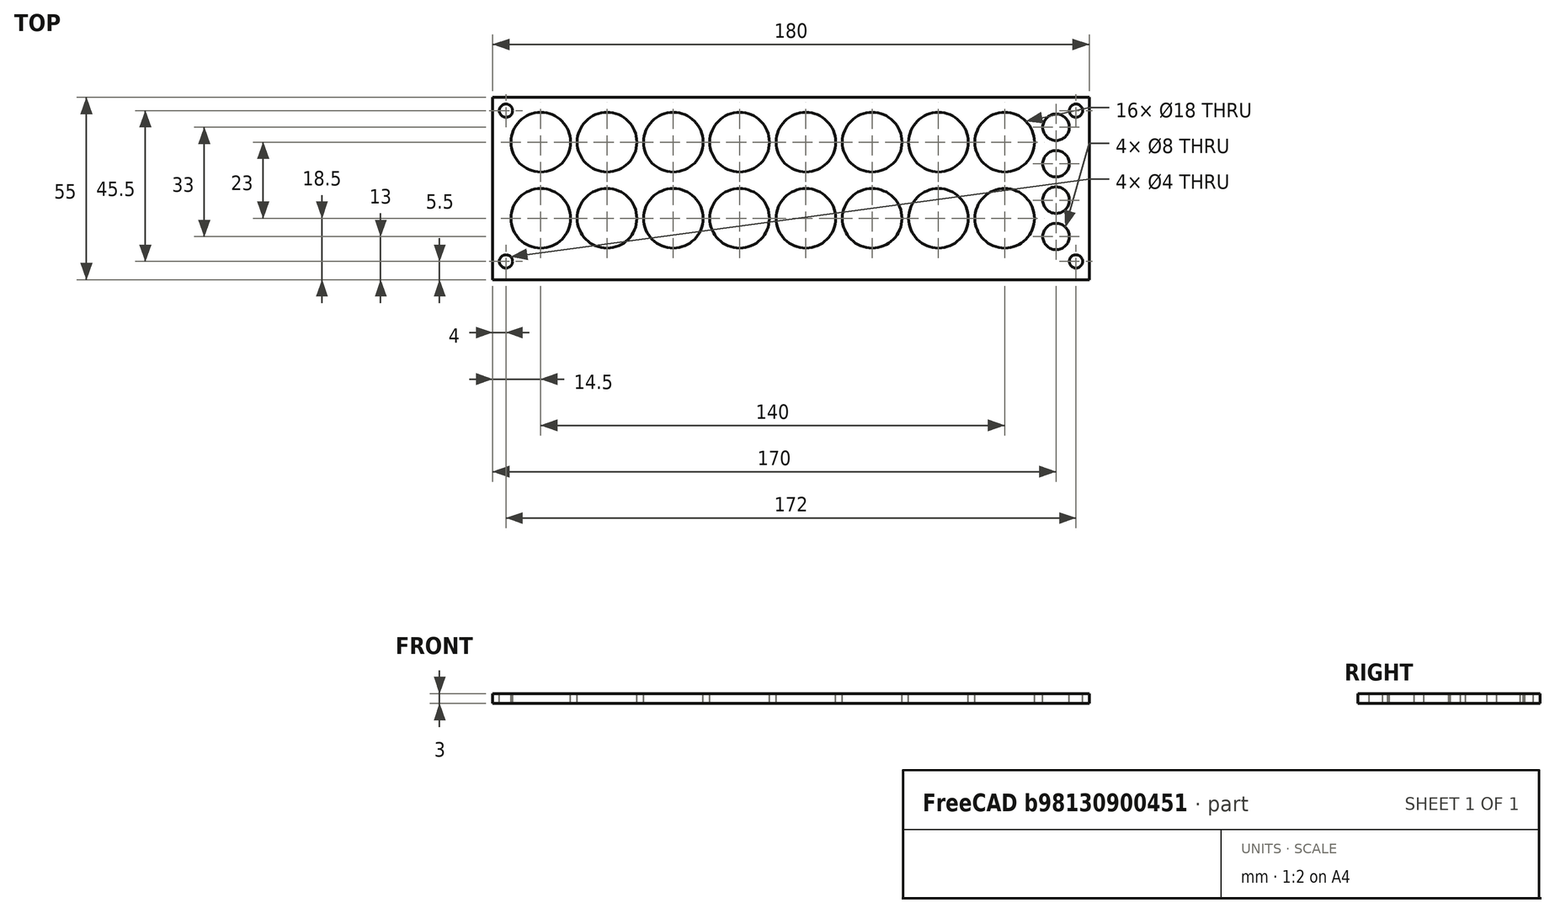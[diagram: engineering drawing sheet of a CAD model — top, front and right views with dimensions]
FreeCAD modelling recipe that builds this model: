
FCSTD DOCUMENT  (FreeCAD 0.17R13509 (Git))
Label: 工具台-2
License: All rights reserved
LicenseURL: http://en.wikipedia.org/wiki/All_rights_reserved
objects: Part::Cylinder×24, Part::Cut×24, Part::Box×1
note: 49 computed .brp shape members not serialized (recipe doc carries the construction recipe); baked Part::Feature solids carry a one-line shape summary decoded from their .brp

FEATURE [Part::Box] Box  label="外壳"
  AttacherType = Attacher::AttachEngine3D
  Height = 3
  Length = 180
  Width = 55
FEATURE [Part::Cylinder] Cylinder  label="圆柱体1.1"
  Angle = 360
  AttacherType = Attacher::AttachEngine3D
  Height = 3
  Placement = pos=(14.5,41.5,0) rot=(0,0,1;0rad)
  Radius = 9
FEATURE [Part::Cylinder] Cylinder001  label="圆柱体1.2"
  Angle = 360
  AttacherType = Attacher::AttachEngine3D
  Height = 3
  Placement = pos=(34.5,41.5,0) rot=(0,0,1;0rad)
  Radius = 9
FEATURE [Part::Cylinder] Cylinder002  label="圆柱体1.3"
  Angle = 360
  AttacherType = Attacher::AttachEngine3D
  Height = 3
  Placement = pos=(54.5,41.5,0) rot=(0,0,1;0rad)
  Radius = 9
FEATURE [Part::Cylinder] Cylinder003  label="圆柱体1.4"
  Angle = 360
  AttacherType = Attacher::AttachEngine3D
  Height = 3
  Placement = pos=(74.5,41.5,0) rot=(0,0,1;0rad)
  Radius = 9
FEATURE [Part::Cylinder] Cylinder004  label="圆柱体2.1"
  Angle = 360
  AttacherType = Attacher::AttachEngine3D
  Height = 3
  Placement = pos=(14.5,18.5,0) rot=(0,0,1;0rad)
  Radius = 9
FEATURE [Part::Cylinder] Cylinder005  label="圆柱体2.2"
  Angle = 360
  AttacherType = Attacher::AttachEngine3D
  Height = 3
  Placement = pos=(34.5,18.5,0) rot=(0,0,1;0rad)
  Radius = 9
FEATURE [Part::Cylinder] Cylinder006  label="圆柱体2.3"
  Angle = 360
  AttacherType = Attacher::AttachEngine3D
  Height = 3
  Placement = pos=(54.5,18.5,0) rot=(0,0,1;0rad)
  Radius = 9
FEATURE [Part::Cylinder] Cylinder007  label="圆柱体2.4"
  Angle = 360
  AttacherType = Attacher::AttachEngine3D
  Height = 3
  Placement = pos=(74.5,18.5,0) rot=(0,0,1;0rad)
  Radius = 9
FEATURE [Part::Cylinder] Cylinder008  label="圆柱体1.5"
  Angle = 360
  AttacherType = Attacher::AttachEngine3D
  Height = 3
  Placement = pos=(94.5,41.5,0) rot=(0,0,1;0rad)
  Radius = 9
FEATURE [Part::Cylinder] Cylinder009  label="圆柱体1.6"
  Angle = 360
  AttacherType = Attacher::AttachEngine3D
  Height = 3
  Placement = pos=(114.5,41.5,0) rot=(0,0,1;0rad)
  Radius = 9
FEATURE [Part::Cylinder] Cylinder010  label="圆柱体1.7"
  Angle = 360
  AttacherType = Attacher::AttachEngine3D
  Height = 3
  Placement = pos=(134.5,41.5,0) rot=(0,0,1;0rad)
  Radius = 9
FEATURE [Part::Cylinder] Cylinder011  label="圆柱体1.8"
  Angle = 360
  AttacherType = Attacher::AttachEngine3D
  Height = 3
  Placement = pos=(154.5,41.5,0) rot=(0,0,1;0rad)
  Radius = 9
FEATURE [Part::Cylinder] Cylinder012  label="圆柱体3.1"
  Angle = 360
  AttacherType = Attacher::AttachEngine3D
  Height = 3
  Placement = pos=(170,46,0) rot=(0,0,1;0rad)
  Radius = 4
FEATURE [Part::Cylinder] Cylinder013  label="圆柱体3.2"
  Angle = 360
  AttacherType = Attacher::AttachEngine3D
  Height = 3
  Placement = pos=(170,35,0) rot=(0,0,1;0rad)
  Radius = 4
FEATURE [Part::Cylinder] Cylinder014  label="圆柱体2.5"
  Angle = 360
  AttacherType = Attacher::AttachEngine3D
  Height = 3
  Placement = pos=(94.5,18.5,0) rot=(0,0,1;0rad)
  Radius = 9
FEATURE [Part::Cylinder] Cylinder015  label="圆柱体2.6"
  Angle = 360
  AttacherType = Attacher::AttachEngine3D
  Height = 3
  Placement = pos=(114.5,18.5,0) rot=(0,0,1;0rad)
  Radius = 9
FEATURE [Part::Cylinder] Cylinder016  label="圆柱体2.7"
  Angle = 360
  AttacherType = Attacher::AttachEngine3D
  Height = 3
  Placement = pos=(134.5,18.5,0) rot=(0,0,1;0rad)
  Radius = 9
FEATURE [Part::Cylinder] Cylinder017  label="圆柱体2.8"
  Angle = 360
  AttacherType = Attacher::AttachEngine3D
  Height = 3
  Placement = pos=(154.5,18.5,0) rot=(0,0,1;0rad)
  Radius = 9
FEATURE [Part::Cylinder] Cylinder018  label="圆柱体3.3"
  Angle = 360
  AttacherType = Attacher::AttachEngine3D
  Height = 3
  Placement = pos=(170,24,0) rot=(0,0,1;0rad)
  Radius = 4
FEATURE [Part::Cylinder] Cylinder019  label="圆柱体3.4"
  Angle = 360
  AttacherType = Attacher::AttachEngine3D
  Height = 3
  Placement = pos=(170,13,0) rot=(0,0,1;0rad)
  Radius = 4
FEATURE [Part::Cylinder] Cylinder020  label="螺孔1.1"
  Angle = 360
  AttacherType = Attacher::AttachEngine3D
  Height = 3
  Placement = pos=(4,5.5,0) rot=(0,0,1;0rad)
  Radius = 2
FEATURE [Part::Cylinder] Cylinder021  label="螺孔1.2"
  Angle = 360
  AttacherType = Attacher::AttachEngine3D
  Height = 3
  Placement = pos=(176,5.5,0) rot=(0,0,1;0rad)
  Radius = 2
FEATURE [Part::Cylinder] Cylinder022  label="螺孔1.3"
  Angle = 360
  AttacherType = Attacher::AttachEngine3D
  Height = 3
  Placement = pos=(4,51,0) rot=(0,0,1;0rad)
  Radius = 2
FEATURE [Part::Cylinder] Cylinder023  label="螺孔1.4"
  Angle = 360
  AttacherType = Attacher::AttachEngine3D
  Height = 3
  Placement = pos=(176,51,0) rot=(0,0,1;0rad)
  Radius = 2
FEATURE [Part::Cut] Cut
  Base = -> Box
  Tool = -> Cylinder
FEATURE [Part::Cut] Cut001
  Base = -> Cut
  Tool = -> Cylinder001
FEATURE [Part::Cut] Cut002
  Base = -> Cut001
  Tool = -> Cylinder002
FEATURE [Part::Cut] Cut003
  Base = -> Cut002
  Tool = -> Cylinder003
FEATURE [Part::Cut] Cut004
  Base = -> Cut003
  Tool = -> Cylinder008
FEATURE [Part::Cut] Cut005
  Base = -> Cut004
  Tool = -> Cylinder009
FEATURE [Part::Cut] Cut006
  Base = -> Cut005
  Tool = -> Cylinder010
FEATURE [Part::Cut] Cut007
  Base = -> Cut006
  Tool = -> Cylinder011
FEATURE [Part::Cut] Cut008
  Base = -> Cut007
  Tool = -> Cylinder004
FEATURE [Part::Cut] Cut009
  Base = -> Cut008
  Tool = -> Cylinder005
FEATURE [Part::Cut] Cut010
  Base = -> Cut009
  Tool = -> Cylinder006
FEATURE [Part::Cut] Cut011
  Base = -> Cut010
  Tool = -> Cylinder007
FEATURE [Part::Cut] Cut012
  Base = -> Cut011
  Tool = -> Cylinder014
FEATURE [Part::Cut] Cut013
  Base = -> Cut012
  Tool = -> Cylinder015
FEATURE [Part::Cut] Cut014
  Base = -> Cut013
  Tool = -> Cylinder016
FEATURE [Part::Cut] Cut015
  Base = -> Cut014
  Tool = -> Cylinder017
FEATURE [Part::Cut] Cut016
  Base = -> Cut015
  Tool = -> Cylinder012
FEATURE [Part::Cut] Cut017
  Base = -> Cut016
  Tool = -> Cylinder013
FEATURE [Part::Cut] Cut018
  Base = -> Cut017
  Tool = -> Cylinder018
FEATURE [Part::Cut] Cut019
  Base = -> Cut018
  Tool = -> Cylinder019
FEATURE [Part::Cut] Cut020
  Base = -> Cut019
  Tool = -> Cylinder020
FEATURE [Part::Cut] Cut021
  Base = -> Cut020
  Tool = -> Cylinder021
FEATURE [Part::Cut] Cut022
  Base = -> Cut021
  Tool = -> Cylinder022
FEATURE [Part::Cut] Cut023
  Base = -> Cut022
  Tool = -> Cylinder023
